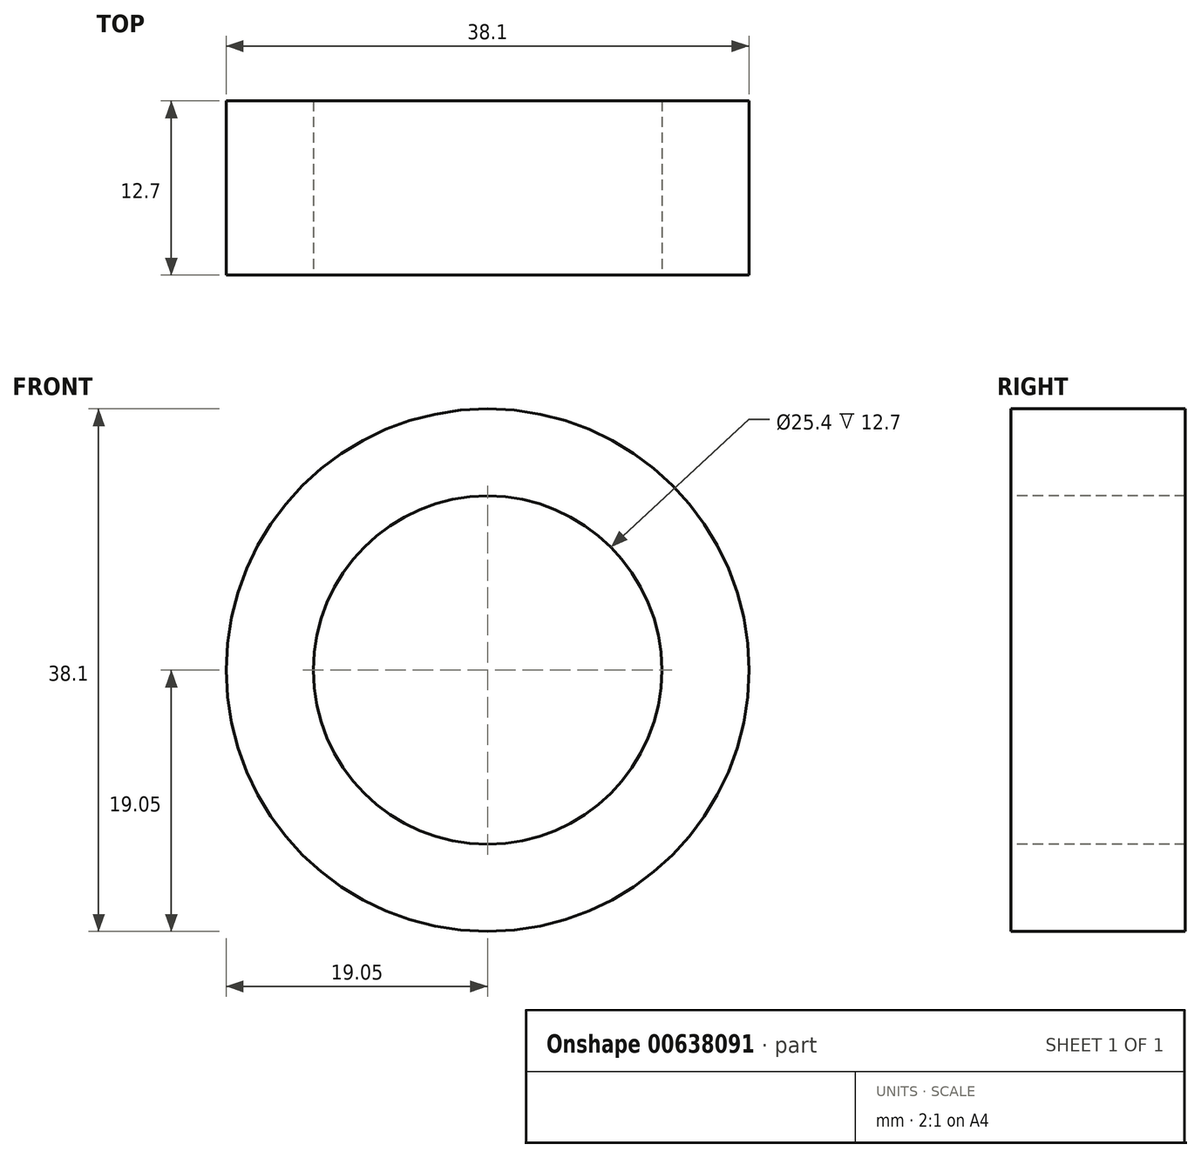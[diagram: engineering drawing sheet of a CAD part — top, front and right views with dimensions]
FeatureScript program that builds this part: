
annotation { "Feature Type Name" : "Feature", "Feature Type Description" : "" }
export const myFeature = defineFeature(function(context is Context, id is Id, definition is map)
    precondition{}
    {
        {
            var Q0;
            Q0=qCreatedBy(makeId("Front.planeOp"),FACE);
            var sketch = newSketch(context, id + "F0", { "sketchPlane" : qUnion([Q0])});
            skCircle(sketch, "E0", {"center": v(0, 0) * mm, "radius": 19.05 * mm});
            skSolve(sketch);
        }
        {
            var Q0;
            Q0=makeQuery(id+"F0.imprint","IMPRINT",FACE,{"disambiguationData":[TD([[makeQuery(id+"F0.imprint","IMPRINT",EDGE,{"derivedFrom":sQuery(id+"F0.wireOp",EDGE,"E0")}),1.0]])]});
            extrude(context, id + "F1", {"entities" : qUnion([Q0]), "depth" : 12.7 * mm, "offsetDistance" : 25.4 * mm});
        }
        {
            var Q0;
            Q0=makeQuery(id+"F1.opExtrude","CAP_FACE",FACE,{"disambiguationData":[OSD([sQuery(id+"F0.wireOp",EDGE,"E0")])],"isStart":false});
            var sketch = newSketch(context, id + "F2", { "sketchPlane" : qUnion([Q0])});
            skPoint(sketch, "E1", {"position": v(0, 0) * mm});
            skSolve(sketch);
        }
        {
            var Q0;
            Q0=sQuery(id+"F2.wireOp",VERTEX,"E1");
            var Q1;
            Q1=makeQuery(id+"F1.opExtrude","SWEPT_BODY",BODY,{"disambiguationData":[OSD([sQuery(id+"F0.wireOp",EDGE,"E0")])]});
            hole(context, id + "F3", {"style" : HoleStyle.SIMPLE, "endStyle" : HoleEndStyle.THROUGH, "holeDiameter" : 25.4 * mm, "majorDiameter" : 6.35 * mm, "isTappedThrough" : true, "tappedDepth" : 12.7 * mm, "tapClearance" : 3, "locations" : qUnion([Q0]), "scope" : qUnion([Q1])});
        }
    });
